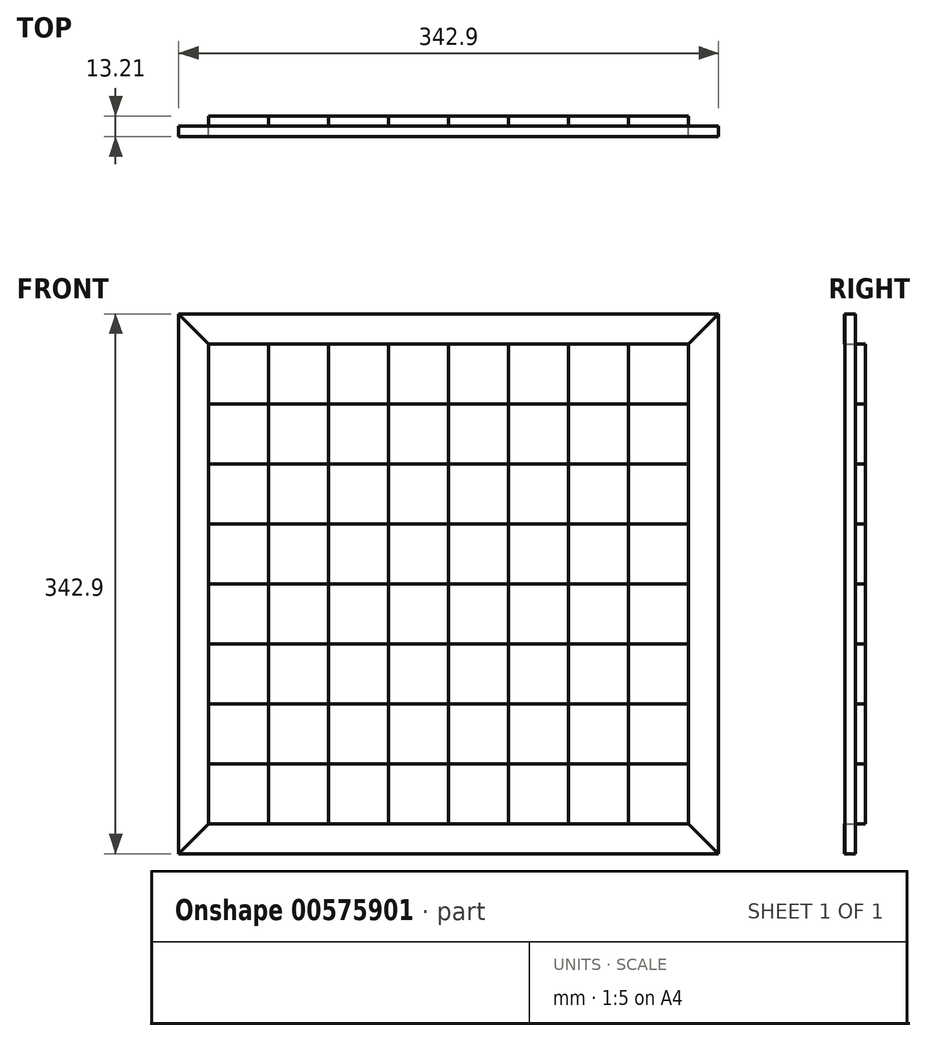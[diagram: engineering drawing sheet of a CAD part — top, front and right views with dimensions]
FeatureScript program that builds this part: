
annotation { "Feature Type Name" : "Feature", "Feature Type Description" : "" }
export const myFeature = defineFeature(function(context is Context, id is Id, definition is map)
    precondition{}
    {
        {
            var Q0;
            Q0=qCreatedBy(makeId("Front.planeOp"),FACE);
            var sketch = newSketch(context, id + "F0", { "sketchPlane" : qUnion([Q0])});
            skLineSegment(sketch, "E0.bottom", {"start": v(-171.45, 171.45) * mm, "end": v(171.45, 171.45) * mm});
            skLineSegment(sketch, "E0.top", {"start": v(-171.45, -171.45) * mm, "end": v(171.45, -171.45) * mm});
            skLineSegment(sketch, "E0.left", {"start": v(-171.45, 171.45) * mm, "end": v(-171.45, -171.45) * mm});
            skLineSegment(sketch, "E0.right", {"start": v(171.45, 171.45) * mm, "end": v(171.45, -171.45) * mm});
            skPoint(sketch, "E0.middle", {"position": v(0, 0) * mm});
            skLineSegment(sketch, "E1.bottom", {"start": v(-152.4, 152.4) * mm, "end": v(152.4, 152.4) * mm});
            skLineSegment(sketch, "E1.top", {"start": v(-152.4, -152.4) * mm, "end": v(152.4, -152.4) * mm});
            skLineSegment(sketch, "E1.left", {"start": v(-152.4, 152.4) * mm, "end": v(-152.4, -152.4) * mm});
            skLineSegment(sketch, "E1.right", {"start": v(152.4, 152.4) * mm, "end": v(152.4, -152.4) * mm});
            skLineSegment(sketch, "E2", {"start": v(-152.4, 152.4) * mm, "end": v(-171.45, 171.45) * mm});
            skLineSegment(sketch, "E3", {"start": v(152.4, 152.4) * mm, "end": v(171.45, 171.45) * mm});
            skLineSegment(sketch, "E4", {"start": v(152.4, -152.4) * mm, "end": v(171.45, -171.45) * mm});
            skLineSegment(sketch, "E5", {"start": v(-152.4, -152.4) * mm, "end": v(-171.45, -171.45) * mm});
            skLineSegment(sketch, "E6", {"start": v(-114.3, -152.4) * mm, "end": v(-114.3, 152.4) * mm});
            skLineSegment(sketch, "E7", {"start": v(-152.4, 114.3) * mm, "end": v(152.4, 114.3) * mm});
            skLineSegment(sketch, "E8.MirrorCS", {"start": v(-76.2, 152.4) * mm, "end": v(-76.2, -152.4) * mm});
            skLineSegment(sketch, "E9.MirrorCS", {"start": v(-38.1, -152.4) * mm, "end": v(-38.1, 152.4) * mm});
            skLineSegment(sketch, "E10.MirrorCS", {"start": v(0, 152.4) * mm, "end": v(0, -152.4) * mm});
            skLineSegment(sketch, "E11.MirrorCS", {"start": v(38.1, -152.4) * mm, "end": v(38.1, 152.4) * mm});
            skLineSegment(sketch, "E12.MirrorCS", {"start": v(76.2, 152.4) * mm, "end": v(76.2, -152.4) * mm});
            skLineSegment(sketch, "E13.MirrorCS", {"start": v(114.3, -152.4) * mm, "end": v(114.3, 152.4) * mm});
            skLineSegment(sketch, "E14.MirrorCS", {"start": v(-152.4, 76.2) * mm, "end": v(152.4, 76.2) * mm});
            skLineSegment(sketch, "E15.MirrorCS", {"start": v(-152.4, 38.1) * mm, "end": v(152.4, 38.1) * mm});
            skLineSegment(sketch, "E16.MirrorCS", {"start": v(-152.4, 0) * mm, "end": v(152.4, 0) * mm});
            skLineSegment(sketch, "E17.MirrorCS", {"start": v(-152.4, -38.1) * mm, "end": v(152.4, -38.1) * mm});
            skLineSegment(sketch, "E18.MirrorCS", {"start": v(-152.4, -76.2) * mm, "end": v(152.4, -76.2) * mm});
            skLineSegment(sketch, "E19.MirrorCS", {"start": v(-152.4, -114.3) * mm, "end": v(152.4, -114.3) * mm});
            skSolve(sketch);
        }
        {
            var Q0;
            {var subQ0=sQuery(id+"F0.wireOp",EDGE,"E15.MirrorCS");var subQ1=sQuery(id+"F0.wireOp",EDGE,"E6");var subQ2=makeQuery(id+"F0.imprint","INTERSECT",VERTEX,{"derivedFrom":[subQ1,subQ0]});Q0=makeQuery(id+"F0.imprint","IMPRINT",FACE,{"disambiguationData":[TD([[makeQuery(id+"F0.imprint","IMPRINT",EDGE,{"disambiguationData":[TD([[subQ2,-1.0]])],"derivedFrom":subQ1}),1.0]])]});}
            var Q1;
            {var subQ0=sQuery(id+"F0.wireOp",EDGE,"E14.MirrorCS");var subQ1=sQuery(id+"F0.wireOp",EDGE,"E6");var subQ2=makeQuery(id+"F0.imprint","INTERSECT",VERTEX,{"derivedFrom":[subQ1,subQ0]});Q1=makeQuery(id+"F0.imprint","IMPRINT",FACE,{"disambiguationData":[TD([[makeQuery(id+"F0.imprint","IMPRINT",EDGE,{"disambiguationData":[TD([[subQ2,-1.0]])],"derivedFrom":subQ1}),-1.0]])]});}
            var Q2;
            {var subQ0=sQuery(id+"F0.wireOp",EDGE,"E14.MirrorCS");var subQ1=sQuery(id+"F0.wireOp",EDGE,"E8.MirrorCS");var subQ2=makeQuery(id+"F0.imprint","INTERSECT",VERTEX,{"derivedFrom":[subQ1,subQ0]});Q2=makeQuery(id+"F0.imprint","IMPRINT",FACE,{"disambiguationData":[TD([[makeQuery(id+"F0.imprint","IMPRINT",EDGE,{"disambiguationData":[TD([[subQ2,-1.0]])],"derivedFrom":subQ1}),1.0]])]});}
            var Q3;
            {var subQ0=sQuery(id+"F0.wireOp",EDGE,"E8.MirrorCS");var subQ1=sQuery(id+"F0.wireOp",EDGE,"E1.bottom");var subQ2=makeQuery(id+"F0.imprint","INTERSECT",VERTEX,{"derivedFrom":[subQ1,subQ0]});Q3=makeQuery(id+"F0.imprint","IMPRINT",FACE,{"disambiguationData":[TD([[makeQuery(id+"F0.imprint","IMPRINT",EDGE,{"disambiguationData":[TD([[subQ2,-1.0]])],"derivedFrom":subQ1}),-1.0]])]});}
            var Q4;
            {var subQ0=sQuery(id+"F0.wireOp",EDGE,"E10.MirrorCS");var subQ1=sQuery(id+"F0.wireOp",EDGE,"E1.bottom");var subQ2=makeQuery(id+"F0.imprint","INTERSECT",VERTEX,{"derivedFrom":[subQ1,subQ0]});Q4=makeQuery(id+"F0.imprint","IMPRINT",FACE,{"disambiguationData":[TD([[makeQuery(id+"F0.imprint","IMPRINT",EDGE,{"disambiguationData":[TD([[subQ2,-1.0]])],"derivedFrom":subQ1}),-1.0]])]});}
            var Q5;
            {var subQ0=sQuery(id+"F0.wireOp",EDGE,"E14.MirrorCS");var subQ1=sQuery(id+"F0.wireOp",EDGE,"E10.MirrorCS");var subQ2=makeQuery(id+"F0.imprint","INTERSECT",VERTEX,{"derivedFrom":[subQ1,subQ0]});Q5=makeQuery(id+"F0.imprint","IMPRINT",FACE,{"disambiguationData":[TD([[makeQuery(id+"F0.imprint","IMPRINT",EDGE,{"disambiguationData":[TD([[subQ2,-1.0]])],"derivedFrom":subQ1}),1.0]])]});}
            var Q6;
            {var subQ0=sQuery(id+"F0.wireOp",EDGE,"E9.MirrorCS");var subQ1=sQuery(id+"F0.wireOp",EDGE,"E7");var subQ2=makeQuery(id+"F0.imprint","INTERSECT",VERTEX,{"derivedFrom":[subQ1,subQ0]});Q6=makeQuery(id+"F0.imprint","IMPRINT",FACE,{"disambiguationData":[TD([[makeQuery(id+"F0.imprint","IMPRINT",EDGE,{"disambiguationData":[TD([[subQ2,-1.0]])],"derivedFrom":subQ1}),-1.0]])]});}
            var Q7;
            {var subQ0=sQuery(id+"F0.wireOp",EDGE,"E11.MirrorCS");var subQ1=sQuery(id+"F0.wireOp",EDGE,"E7");var subQ2=makeQuery(id+"F0.imprint","INTERSECT",VERTEX,{"derivedFrom":[subQ1,subQ0]});Q7=makeQuery(id+"F0.imprint","IMPRINT",FACE,{"disambiguationData":[TD([[makeQuery(id+"F0.imprint","IMPRINT",EDGE,{"disambiguationData":[TD([[subQ2,-1.0]])],"derivedFrom":subQ1}),-1.0]])]});}
            var Q8;
            {var subQ0=sQuery(id+"F0.wireOp",EDGE,"E7");var subQ1=sQuery(id+"F0.wireOp",EDGE,"E1.right");var subQ2=makeQuery(id+"F0.imprint","INTERSECT",VERTEX,{"derivedFrom":[subQ1,subQ0]});Q8=makeQuery(id+"F0.imprint","IMPRINT",FACE,{"disambiguationData":[TD([[makeQuery(id+"F0.imprint","IMPRINT",EDGE,{"disambiguationData":[TD([[subQ2,-1.0]])],"derivedFrom":subQ1}),-1.0]])]});}
            var Q9;
            {var subQ0=sQuery(id+"F0.wireOp",EDGE,"E12.MirrorCS");var subQ1=sQuery(id+"F0.wireOp",EDGE,"E1.bottom");var subQ2=makeQuery(id+"F0.imprint","INTERSECT",VERTEX,{"derivedFrom":[subQ1,subQ0]});Q9=makeQuery(id+"F0.imprint","IMPRINT",FACE,{"disambiguationData":[TD([[makeQuery(id+"F0.imprint","IMPRINT",EDGE,{"disambiguationData":[TD([[subQ2,-1.0]])],"derivedFrom":subQ1}),-1.0]])]});}
            var Q10;
            {var subQ0=sQuery(id+"F0.wireOp",EDGE,"E14.MirrorCS");var subQ1=sQuery(id+"F0.wireOp",EDGE,"E12.MirrorCS");var subQ2=makeQuery(id+"F0.imprint","INTERSECT",VERTEX,{"derivedFrom":[subQ1,subQ0]});Q10=makeQuery(id+"F0.imprint","IMPRINT",FACE,{"disambiguationData":[TD([[makeQuery(id+"F0.imprint","IMPRINT",EDGE,{"disambiguationData":[TD([[subQ2,-1.0]])],"derivedFrom":subQ1}),1.0]])]});}
            var Q11;
            {var subQ0=sQuery(id+"F0.wireOp",EDGE,"E17.MirrorCS");var subQ1=sQuery(id+"F0.wireOp",EDGE,"E6");var subQ2=makeQuery(id+"F0.imprint","INTERSECT",VERTEX,{"derivedFrom":[subQ1,subQ0]});Q11=makeQuery(id+"F0.imprint","IMPRINT",FACE,{"disambiguationData":[TD([[makeQuery(id+"F0.imprint","IMPRINT",EDGE,{"disambiguationData":[TD([[subQ2,-1.0]])],"derivedFrom":subQ1}),1.0]])]});}
            var Q12;
            {var subQ0=sQuery(id+"F0.wireOp",EDGE,"E19.MirrorCS");var subQ1=sQuery(id+"F0.wireOp",EDGE,"E6");var subQ2=makeQuery(id+"F0.imprint","INTERSECT",VERTEX,{"derivedFrom":[subQ1,subQ0]});Q12=makeQuery(id+"F0.imprint","IMPRINT",FACE,{"disambiguationData":[TD([[makeQuery(id+"F0.imprint","IMPRINT",EDGE,{"disambiguationData":[TD([[subQ2,-1.0]])],"derivedFrom":subQ1}),1.0]])]});}
            var Q13;
            {var subQ0=sQuery(id+"F0.wireOp",EDGE,"E6");var subQ1=sQuery(id+"F0.wireOp",EDGE,"E1.top");var subQ2=makeQuery(id+"F0.imprint","INTERSECT",VERTEX,{"derivedFrom":[subQ1,subQ0]});Q13=makeQuery(id+"F0.imprint","IMPRINT",FACE,{"disambiguationData":[TD([[makeQuery(id+"F0.imprint","IMPRINT",EDGE,{"disambiguationData":[TD([[subQ2,-1.0]])],"derivedFrom":subQ1}),1.0]])]});}
            var Q14;
            {var subQ0=sQuery(id+"F0.wireOp",EDGE,"E18.MirrorCS");var subQ1=sQuery(id+"F0.wireOp",EDGE,"E6");var subQ2=makeQuery(id+"F0.imprint","INTERSECT",VERTEX,{"derivedFrom":[subQ1,subQ0]});Q14=makeQuery(id+"F0.imprint","IMPRINT",FACE,{"disambiguationData":[TD([[makeQuery(id+"F0.imprint","IMPRINT",EDGE,{"disambiguationData":[TD([[subQ2,-1.0]])],"derivedFrom":subQ1}),-1.0]])]});}
            var Q15;
            {var subQ0=sQuery(id+"F0.wireOp",EDGE,"E16.MirrorCS");var subQ1=sQuery(id+"F0.wireOp",EDGE,"E6");var subQ2=makeQuery(id+"F0.imprint","INTERSECT",VERTEX,{"derivedFrom":[subQ1,subQ0]});Q15=makeQuery(id+"F0.imprint","IMPRINT",FACE,{"disambiguationData":[TD([[makeQuery(id+"F0.imprint","IMPRINT",EDGE,{"disambiguationData":[TD([[subQ2,-1.0]])],"derivedFrom":subQ1}),-1.0]])]});}
            var Q16;
            {var subQ0=sQuery(id+"F0.wireOp",EDGE,"E16.MirrorCS");var subQ1=sQuery(id+"F0.wireOp",EDGE,"E8.MirrorCS");var subQ2=makeQuery(id+"F0.imprint","INTERSECT",VERTEX,{"derivedFrom":[subQ1,subQ0]});Q16=makeQuery(id+"F0.imprint","IMPRINT",FACE,{"disambiguationData":[TD([[makeQuery(id+"F0.imprint","IMPRINT",EDGE,{"disambiguationData":[TD([[subQ2,-1.0]])],"derivedFrom":subQ1}),1.0]])]});}
            var Q17;
            {var subQ0=sQuery(id+"F0.wireOp",EDGE,"E18.MirrorCS");var subQ1=sQuery(id+"F0.wireOp",EDGE,"E8.MirrorCS");var subQ2=makeQuery(id+"F0.imprint","INTERSECT",VERTEX,{"derivedFrom":[subQ1,subQ0]});Q17=makeQuery(id+"F0.imprint","IMPRINT",FACE,{"disambiguationData":[TD([[makeQuery(id+"F0.imprint","IMPRINT",EDGE,{"disambiguationData":[TD([[subQ2,-1.0]])],"derivedFrom":subQ1}),1.0]])]});}
            var Q18;
            {var subQ0=sQuery(id+"F0.wireOp",EDGE,"E18.MirrorCS");var subQ1=sQuery(id+"F0.wireOp",EDGE,"E9.MirrorCS");var subQ2=makeQuery(id+"F0.imprint","INTERSECT",VERTEX,{"derivedFrom":[subQ1,subQ0]});Q18=makeQuery(id+"F0.imprint","IMPRINT",FACE,{"disambiguationData":[TD([[makeQuery(id+"F0.imprint","IMPRINT",EDGE,{"disambiguationData":[TD([[subQ2,-1.0]])],"derivedFrom":subQ1}),-1.0]])]});}
            var Q19;
            {var subQ0=sQuery(id+"F0.wireOp",EDGE,"E16.MirrorCS");var subQ1=sQuery(id+"F0.wireOp",EDGE,"E9.MirrorCS");var subQ2=makeQuery(id+"F0.imprint","INTERSECT",VERTEX,{"derivedFrom":[subQ1,subQ0]});Q19=makeQuery(id+"F0.imprint","IMPRINT",FACE,{"disambiguationData":[TD([[makeQuery(id+"F0.imprint","IMPRINT",EDGE,{"disambiguationData":[TD([[subQ2,-1.0]])],"derivedFrom":subQ1}),-1.0]])]});}
            var Q20;
            {var subQ0=sQuery(id+"F0.wireOp",EDGE,"E16.MirrorCS");var subQ1=sQuery(id+"F0.wireOp",EDGE,"E10.MirrorCS");var subQ2=makeQuery(id+"F0.imprint","INTERSECT",VERTEX,{"derivedFrom":[subQ1,subQ0]});Q20=makeQuery(id+"F0.imprint","IMPRINT",FACE,{"disambiguationData":[TD([[makeQuery(id+"F0.imprint","IMPRINT",EDGE,{"disambiguationData":[TD([[subQ2,-1.0]])],"derivedFrom":subQ1}),1.0]])]});}
            var Q21;
            {var subQ0=sQuery(id+"F0.wireOp",EDGE,"E18.MirrorCS");var subQ1=sQuery(id+"F0.wireOp",EDGE,"E10.MirrorCS");var subQ2=makeQuery(id+"F0.imprint","INTERSECT",VERTEX,{"derivedFrom":[subQ1,subQ0]});Q21=makeQuery(id+"F0.imprint","IMPRINT",FACE,{"disambiguationData":[TD([[makeQuery(id+"F0.imprint","IMPRINT",EDGE,{"disambiguationData":[TD([[subQ2,-1.0]])],"derivedFrom":subQ1}),1.0]])]});}
            var Q22;
            {var subQ0=sQuery(id+"F0.wireOp",EDGE,"E11.MirrorCS");var subQ1=sQuery(id+"F0.wireOp",EDGE,"E1.top");var subQ2=makeQuery(id+"F0.imprint","INTERSECT",VERTEX,{"derivedFrom":[subQ1,subQ0]});Q22=makeQuery(id+"F0.imprint","IMPRINT",FACE,{"disambiguationData":[TD([[makeQuery(id+"F0.imprint","IMPRINT",EDGE,{"disambiguationData":[TD([[subQ2,-1.0]])],"derivedFrom":subQ1}),1.0]])]});}
            var Q23;
            {var subQ0=sQuery(id+"F0.wireOp",EDGE,"E18.MirrorCS");var subQ1=sQuery(id+"F0.wireOp",EDGE,"E11.MirrorCS");var subQ2=makeQuery(id+"F0.imprint","INTERSECT",VERTEX,{"derivedFrom":[subQ1,subQ0]});Q23=makeQuery(id+"F0.imprint","IMPRINT",FACE,{"disambiguationData":[TD([[makeQuery(id+"F0.imprint","IMPRINT",EDGE,{"disambiguationData":[TD([[subQ2,-1.0]])],"derivedFrom":subQ1}),-1.0]])]});}
            var Q24;
            {var subQ0=sQuery(id+"F0.wireOp",EDGE,"E16.MirrorCS");var subQ1=sQuery(id+"F0.wireOp",EDGE,"E11.MirrorCS");var subQ2=makeQuery(id+"F0.imprint","INTERSECT",VERTEX,{"derivedFrom":[subQ1,subQ0]});Q24=makeQuery(id+"F0.imprint","IMPRINT",FACE,{"disambiguationData":[TD([[makeQuery(id+"F0.imprint","IMPRINT",EDGE,{"disambiguationData":[TD([[subQ2,-1.0]])],"derivedFrom":subQ1}),-1.0]])]});}
            var Q25;
            {var subQ0=sQuery(id+"F0.wireOp",EDGE,"E16.MirrorCS");var subQ1=sQuery(id+"F0.wireOp",EDGE,"E12.MirrorCS");var subQ2=makeQuery(id+"F0.imprint","INTERSECT",VERTEX,{"derivedFrom":[subQ1,subQ0]});Q25=makeQuery(id+"F0.imprint","IMPRINT",FACE,{"disambiguationData":[TD([[makeQuery(id+"F0.imprint","IMPRINT",EDGE,{"disambiguationData":[TD([[subQ2,-1.0]])],"derivedFrom":subQ1}),1.0]])]});}
            var Q26;
            {var subQ0=sQuery(id+"F0.wireOp",EDGE,"E18.MirrorCS");var subQ1=sQuery(id+"F0.wireOp",EDGE,"E12.MirrorCS");var subQ2=makeQuery(id+"F0.imprint","INTERSECT",VERTEX,{"derivedFrom":[subQ1,subQ0]});Q26=makeQuery(id+"F0.imprint","IMPRINT",FACE,{"disambiguationData":[TD([[makeQuery(id+"F0.imprint","IMPRINT",EDGE,{"disambiguationData":[TD([[subQ2,-1.0]])],"derivedFrom":subQ1}),1.0]])]});}
            var Q27;
            {var subQ0=sQuery(id+"F0.wireOp",EDGE,"E17.MirrorCS");var subQ1=sQuery(id+"F0.wireOp",EDGE,"E1.right");var subQ2=makeQuery(id+"F0.imprint","INTERSECT",VERTEX,{"derivedFrom":[subQ1,subQ0]});Q27=makeQuery(id+"F0.imprint","IMPRINT",FACE,{"disambiguationData":[TD([[makeQuery(id+"F0.imprint","IMPRINT",EDGE,{"disambiguationData":[TD([[subQ2,-1.0]])],"derivedFrom":subQ1}),-1.0]])]});}
            var Q28;
            {var subQ0=sQuery(id+"F0.wireOp",EDGE,"E15.MirrorCS");var subQ1=sQuery(id+"F0.wireOp",EDGE,"E1.right");var subQ2=makeQuery(id+"F0.imprint","INTERSECT",VERTEX,{"derivedFrom":[subQ1,subQ0]});Q28=makeQuery(id+"F0.imprint","IMPRINT",FACE,{"disambiguationData":[TD([[makeQuery(id+"F0.imprint","IMPRINT",EDGE,{"disambiguationData":[TD([[subQ2,-1.0]])],"derivedFrom":subQ1}),-1.0]])]});}
            var Q29;
            {var subQ1=sQuery(id+"F0.wireOp",EDGE,"E1.top");var subQ3=sQuery(id+"F0.wireOp",EDGE,"E13.MirrorCS");var subQ4=makeQuery(id+"F0.imprint","INTERSECT",VERTEX,{"derivedFrom":[subQ1,subQ3]});Q29=makeQuery(id+"F0.imprint","IMPRINT",FACE,{"disambiguationData":[TD([[makeQuery(id+"F0.imprint","IMPRINT",EDGE,{"disambiguationData":[TD([[subQ4,-1.0]])],"derivedFrom":subQ3}),-1.0]])]});}
            var Q30;
            {var subQ0=sQuery(id+"F0.wireOp",EDGE,"E9.MirrorCS");var subQ1=sQuery(id+"F0.wireOp",EDGE,"E1.top");var subQ2=makeQuery(id+"F0.imprint","INTERSECT",VERTEX,{"derivedFrom":[subQ1,subQ0]});Q30=makeQuery(id+"F0.imprint","IMPRINT",FACE,{"disambiguationData":[TD([[makeQuery(id+"F0.imprint","IMPRINT",EDGE,{"disambiguationData":[TD([[subQ2,-1.0]])],"derivedFrom":subQ1}),1.0]])]});}
            var Q31;
            {var subQ1=sQuery(id+"F0.wireOp",EDGE,"E1.bottom");var subQ3=sQuery(id+"F0.wireOp",EDGE,"E6");var subQ4=makeQuery(id+"F0.imprint","INTERSECT",VERTEX,{"derivedFrom":[subQ1,subQ3]});Q31=makeQuery(id+"F0.imprint","IMPRINT",FACE,{"disambiguationData":[TD([[makeQuery(id+"F0.imprint","IMPRINT",EDGE,{"disambiguationData":[TD([[subQ4,1.0]])],"derivedFrom":subQ3}),1.0]])]});}
            extrude(context, id + "F1", {"entities" : qUnion([Q0, Q1, Q2, Q3, Q4, Q5, Q6, Q7, Q8, Q9, Q10, Q11, Q12, Q13, Q14, Q15, Q16, Q17, Q18, Q19, Q20, Q21, Q22, Q23, Q24, Q25, Q26, Q27, Q28, Q29, Q30, Q31]), "oppositeDirection" : true, "depth" : 6.35 * mm, "offsetDistance" : 25.4 * mm});
        }
        {
            var Q0;
            Q0=makeQuery(id+"F0.imprint","IMPRINT",FACE,{"disambiguationData":[TD([[makeQuery(id+"F0.imprint","IMPRINT",EDGE,{"derivedFrom":sQuery(id+"F0.wireOp",EDGE,"E0.left")}),1.0]])]});
            var Q1;
            Q1=makeQuery(id+"F0.imprint","IMPRINT",FACE,{"disambiguationData":[TD([[makeQuery(id+"F0.imprint","IMPRINT",EDGE,{"derivedFrom":sQuery(id+"F0.wireOp",EDGE,"E0.right")}),-1.0]])]});
            extrude(context, id + "F2", {"entities" : qUnion([Q0, Q1]), "depth" : 6.6 * mm, "offsetDistance" : 25.4 * mm});
        }
        {
            var Q0;
            Q0=makeQuery(id+"F0.imprint","IMPRINT",FACE,{"disambiguationData":[TD([[makeQuery(id+"F0.imprint","IMPRINT",EDGE,{"derivedFrom":sQuery(id+"F0.wireOp",EDGE,"E0.top")}),1.0]])]});
            var Q1;
            Q1=makeQuery(id+"F0.imprint","IMPRINT",FACE,{"disambiguationData":[TD([[makeQuery(id+"F0.imprint","IMPRINT",EDGE,{"derivedFrom":sQuery(id+"F0.wireOp",EDGE,"E0.bottom")}),-1.0]])]});
            extrude(context, id + "F3", {"entities" : qUnion([Q0, Q1]), "depth" : 6.86 * mm, "offsetDistance" : 25.4 * mm});
        }
    });
